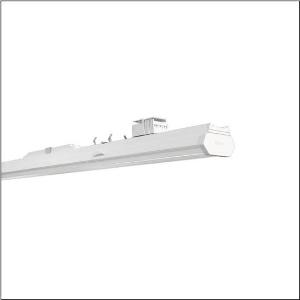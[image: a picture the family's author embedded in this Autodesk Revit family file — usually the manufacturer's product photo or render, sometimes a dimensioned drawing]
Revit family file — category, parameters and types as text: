
# Revit family: licross_r__11_protected_mo_51tp11cn58xf_4d9e
name_source: partatom
category: Lighting Fixtures
units: mm (PartAtom-declared; Revit-internal decimal feet)

## family parameters
Cut with Voids When Loaded = No
Host = Face
Light Source = No
Part Type = Normal
Room Calculation Point = No
Round Connector Dimension = Use Diameter
Shared = No

## types (1)
- --- (1 x LED, 8150 lm, 49 W, 5000K)
    Apparent Load = 49 VA
    CIE Flux Codes = 83 94 98 100 100
    Color Rendering = 80
    Color Temperature = 5000K
    Default Elevation = 1800 mm
    Description = Licross® 11 Protected MO, luminaire insert, of sheet steel, galvanised, coil coated, white, length: 1.500mm, width: 90mm, height: 101mm, LED rated luminous flux: 8.150lm, light colour: 850, SDCM (Standard Deviation of Colour Matching)MacAdam ≤ 3 SDCM (initial), control gear: ON/OFF Multilumen, CLOi, control gear: ECG Multilumen, with plug, 3-pole, with phase selection, mains connection: 220..240V, AC, 50/60Hz, start of lifetime: 49W, end of service life: 54W, internal wiring halogen-free, primary optical cover: cover, of PMMA, light emission: direct distribution, primary light characteristic: symmetric, protection rating (complete): IP64, insulation class (complete): insulation class I (protective earthing), certification: CE, ENEC, VDE, UKCA, protection symbol: D if used in an environment with conductive dust loads with corresponding accessories, impact resistance: IK06, permissible ambient temperature for indoor applications: -35..+40°C, corresponds to IFS (International Featured Standards) requirements for safety and quality in the food industry, reducing of maximum allowable ambient temperature of 5°C with ceiling mounting, LABS conformity tested according to VDMA 24364:2018-05, packaging unit: 1 piece
    Height = 92 mm
    Lamp = 1 x LED
    Lamp Light Flux = 8150 lm
    Lamp Power = 49 W
    Lamp count = 1
    Length = 1500 mm
    Luminous efficacy = 166 lm/W
    Manufacturer = Siteco
    ModVariant = No
    Model = 51TP11CN58XF
    Mounting Place = Ceiling
    Mounting Type = Pendant
    Number of Poles = 1
    OnlyDefault = Yes
    Power Factor = 1
    Product Name = Licross® 11 Protected MO
    Product group = luminaire insert | ceiling pendant
    ProductGroupID = 901
    Protection Class = Protection class I
    Protection Degree = IP 64
    RLX_Detail_Level = 1
    RLX_Emergency_Light_Flux = 0 lm
    RLX_Emergency_Type = 0
    RLX_Emergency_Type_DB = No
    RlxData = <blob elided: 21901 chars, md5=47d2e8b8>
    Socket = socket
    Standby Power = 0 W
    System Light Flux = 8150 lm
    System Power = 49 W
    Type Comments = factory setting: luminous flux: 100 % | (A | C | E) | 111 mA
    Type Image = l_1256148.jpg
    URL = http://relux.com
    VarID = @adj_199761
    Voltage = 0 V
    Weight = 0.00 kg
    Width = 88 mm

## geometry (parser evidence)
native form markers: Blend x4, Sweep x10
no freeform markers — native parametric forms only
